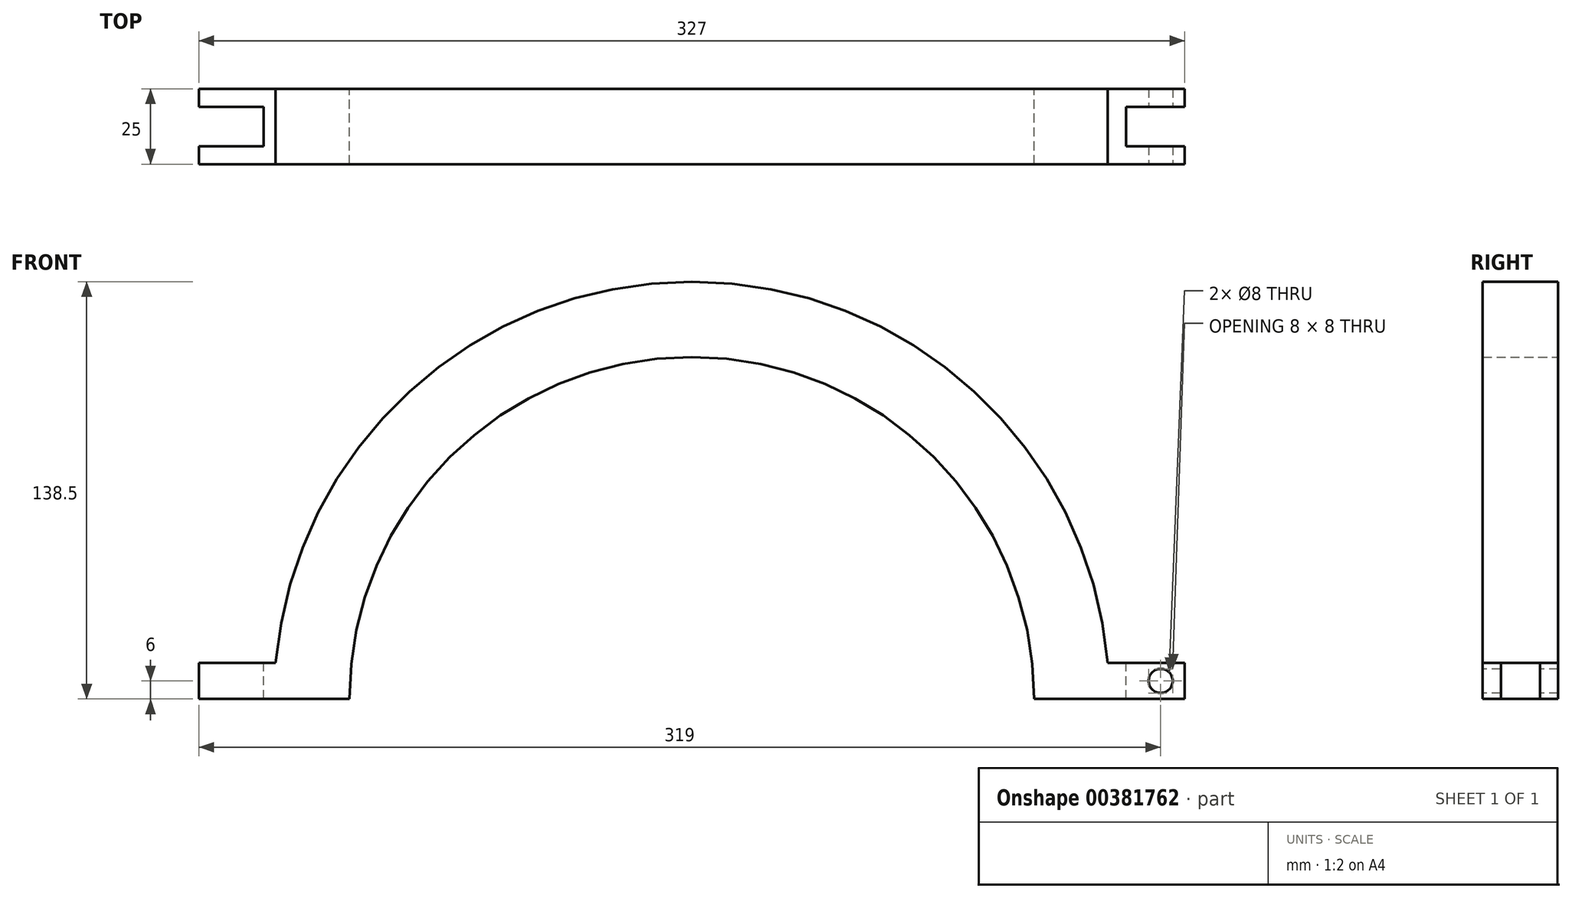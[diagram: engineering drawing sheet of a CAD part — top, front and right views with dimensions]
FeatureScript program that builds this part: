
annotation { "Feature Type Name" : "Feature", "Feature Type Description" : "" }
export const myFeature = defineFeature(function(context is Context, id is Id, definition is map)
    precondition{}
    {
        {
            var Q0;
            Q0=qCreatedBy(makeId("Front.planeOp"),FACE);
            var sketch = newSketch(context, id + "F0", { "sketchPlane" : qUnion([Q0])});
            skArc(sketch, "E0", {"start": v(113.5, 0) * mm, "mid": v(0, 113.5) * mm, "end": v(-113.5, 0) * mm});
            skArc(sketch, "E1.0", {"start": v(138.5, 0) * mm, "mid": v(0, 138.5) * mm, "end": v(-138.5, 0) * mm});
            skLineSegment(sketch, "E2", {"start": v(-138.5, 0) * mm, "end": v(138.5, 0) * mm});
            skLineSegment(sketch, "E3.top", {"start": v(137.98, 12) * mm, "end": v(163.5, 12) * mm});
            skLineSegment(sketch, "E3.right", {"start": v(163.5, 0) * mm, "end": v(163.5, 12) * mm});
            skPoint(sketch, "E3.middle", {"position": v(138.5, 0) * mm});
            skLineSegment(sketch, "E4", {"start": v(138.5, 0) * mm, "end": v(163.5, 0) * mm});
            skPoint(sketch, "E5.middle", {"position": v(-138.5, 0) * mm});
            skLineSegment(sketch, "E6", {"start": v(-138.5, 0) * mm, "end": v(-163.5, 0) * mm});
            skLineSegment(sketch, "E7", {"start": v(-163.5, 0) * mm, "end": v(-163.5, 12) * mm});
            skLineSegment(sketch, "E8", {"start": v(-163.5, 12) * mm, "end": v(-137.98, 12) * mm});
            skSolve(sketch);
        }
        {
            var Q0;
            {var subQ2=sQuery(id+"F0.wireOp",EDGE,"E3.top");Q0=makeQuery(id+"F0.imprint","IMPRINT",FACE,{"disambiguationData":[TD([[makeQuery(id+"F0.imprint","IMPRINT",EDGE,{"derivedFrom":subQ2}),-1.0]])]});}
            var Q1;
            {var subQ0=sQuery(id+"F0.wireOp",EDGE,"E6");Q1=makeQuery(id+"F0.imprint","IMPRINT",FACE,{"disambiguationData":[TD([[makeQuery(id+"F0.imprint","IMPRINT",EDGE,{"derivedFrom":subQ0}),-1.0]])]});}
            var Q2;
            {var subQ6=sQuery(id+"F0.wireOp",EDGE,"E0");Q2=makeQuery(id+"F0.imprint","IMPRINT",FACE,{"disambiguationData":[TD([[makeQuery(id+"F0.imprint","IMPRINT",EDGE,{"derivedFrom":subQ6}),-1.0]])]});}
            extrude(context, id + "F1", {"entities" : qUnion([Q0, Q1, Q2]), "endBound" : BoundingType.SYMMETRIC, "depth" : 25 * mm});
        }
        {
            var Q0;
            Q0=makeQuery(id+"F1.opExtrude","SWEPT_FACE",FACE,{"disambiguationData":[OSD([sQuery(id+"F0.wireOp",EDGE,"E3.top")])]});
            var sketch = newSketch(context, id + "F2", { "sketchPlane" : qUnion([Q0])});
            skLineSegment(sketch, "E9.bottom", {"start": v(163.5, 6.5) * mm, "end": v(143.98, 6.5) * mm});
            skLineSegment(sketch, "E9.top", {"start": v(163.5, -6.5) * mm, "end": v(143.98, -6.5) * mm});
            skLineSegment(sketch, "E9.left", {"start": v(163.5, 6.5) * mm, "end": v(163.5, -6.5) * mm});
            skLineSegment(sketch, "E9.right", {"start": v(143.98, 6.5) * mm, "end": v(143.98, -6.5) * mm});
            skSolve(sketch);
        }
        {
            var Q0;
            Q0 = qSketchRegion(id + "F2", true);
            extrude(context, id + "F3", {"entities" : qUnion([Q0]), "operationType" : NewBodyOperationType.REMOVE, "endBound" : BoundingType.THROUGH_ALL, "oppositeDirection" : true, "depth" : 25 * mm});
        }
        {
            var Q0;
            Q0=makeQuery(id+"F1.opExtrude","SWEPT_FACE",FACE,{"disambiguationData":[OSD([sQuery(id+"F0.wireOp",EDGE,"E8")])]});
            var sketch = newSketch(context, id + "F4", { "sketchPlane" : qUnion([Q0])});
            skLineSegment(sketch, "E10.bottom", {"start": v(-163.5, 6.5) * mm, "end": v(-141.98, 6.5) * mm});
            skLineSegment(sketch, "E10.top", {"start": v(-163.5, -6.5) * mm, "end": v(-141.98, -6.5) * mm});
            skLineSegment(sketch, "E10.left", {"start": v(-163.5, 6.5) * mm, "end": v(-163.5, -6.5) * mm});
            skLineSegment(sketch, "E10.right", {"start": v(-141.98, 6.5) * mm, "end": v(-141.98, -6.5) * mm});
            skSolve(sketch);
        }
        {
            var Q0;
            Q0 = qSketchRegion(id + "F4", true);
            extrude(context, id + "F5", {"entities" : qUnion([Q0]), "operationType" : NewBodyOperationType.REMOVE, "endBound" : BoundingType.THROUGH_ALL, "oppositeDirection" : true, "depth" : 25 * mm});
        }
        {
            var Q0;
            Q0=makeQuery(id+"F1.opExtrude","CAP_FACE",FACE,{"disambiguationData":[OSD([sQuery(id+"F0.wireOp",EDGE,"E0"),sQuery(id+"F0.wireOp",EDGE,"E1.0"),sQuery(id+"F0.wireOp",EDGE,"E2"),sQuery(id+"F0.wireOp",EDGE,"E3.top"),sQuery(id+"F0.wireOp",EDGE,"E3.right"),sQuery(id+"F0.wireOp",EDGE,"E4"),sQuery(id+"F0.wireOp",EDGE,"E6"),sQuery(id+"F0.wireOp",EDGE,"E7"),sQuery(id+"F0.wireOp",EDGE,"E8")])],"isStart":false});
            var sketch = newSketch(context, id + "F6", { "sketchPlane" : qUnion([Q0])});
            skCircle(sketch, "E11", {"center": v(155.5, 6) * mm, "radius": 4 * mm});
            skSolve(sketch);
        }
        {
            var Q0;
            Q0 = qSketchRegion(id + "F6", true);
            extrude(context, id + "F7", {"entities" : qUnion([Q0]), "operationType" : NewBodyOperationType.REMOVE, "endBound" : BoundingType.THROUGH_ALL, "oppositeDirection" : true, "depth" : 25 * mm});
        }
    });
